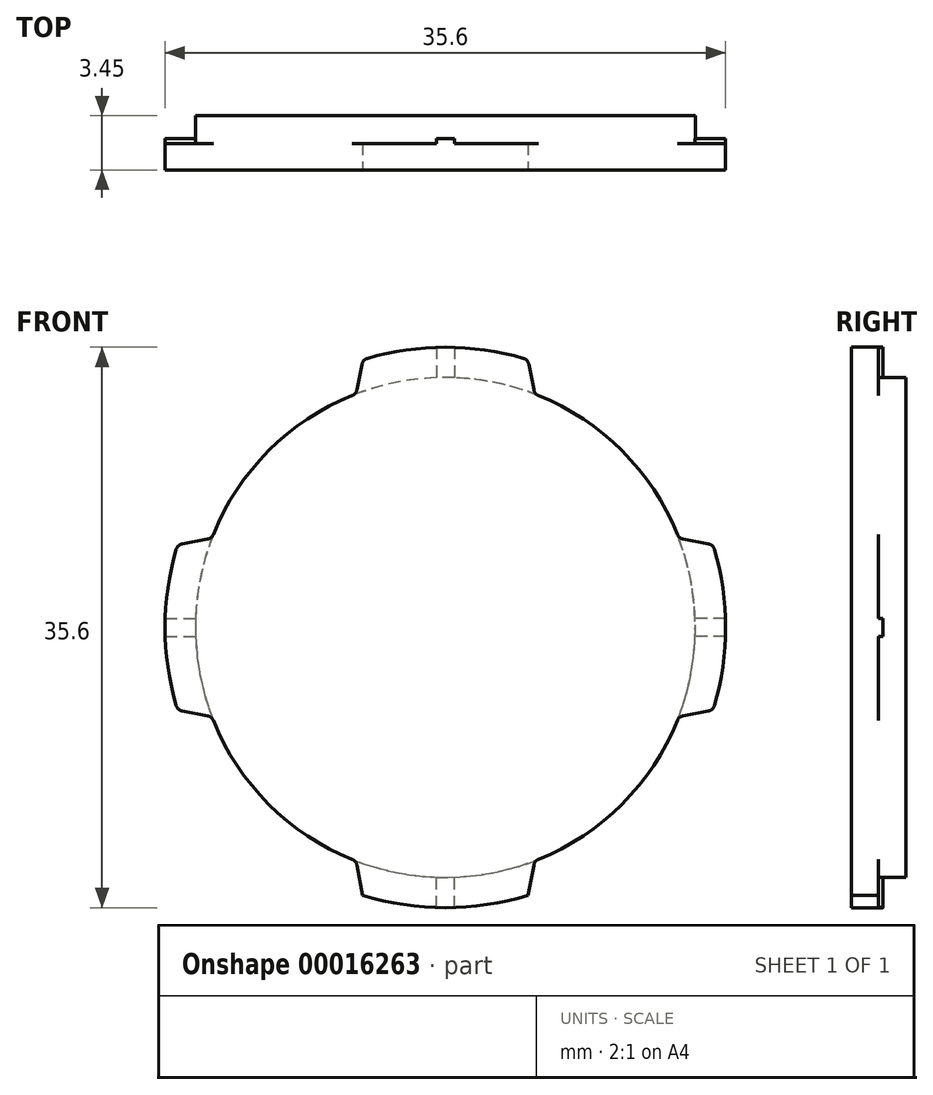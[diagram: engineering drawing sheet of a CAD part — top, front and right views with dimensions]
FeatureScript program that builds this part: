
annotation { "Feature Type Name" : "Feature", "Feature Type Description" : "" }
export const myFeature = defineFeature(function(context is Context, id is Id, definition is map)
    precondition{}
    {
        {
            var Q0;
            Q0=qCreatedBy(makeId("Front.planeOp"),FACE);
            var sketch = newSketch(context, id + "F0", { "sketchPlane" : qUnion([Q0])});
            skCircle(sketch, "E0", {"center": v(0, 0) * mm, "radius": 15.88 * mm});
            skSolve(sketch);
        }
        {
            var Q0;
            Q0=makeQuery(id+"F0.imprint","IMPRINT",FACE,{"disambiguationData":[TD([[makeQuery(id+"F0.imprint","IMPRINT",EDGE,{"derivedFrom":sQuery(id+"F0.wireOp",EDGE,"E0")}),1.0]])]});
            extrude(context, id + "F1", {"entities" : qUnion([Q0]), "depth" : 1.75 * mm});
        }
        {
            var Q0;
            Q0=makeQuery(id+"F1.opExtrude","CAP_FACE",FACE,{"disambiguationData":[OSD([sQuery(id+"F0.wireOp",EDGE,"E0")])],"isStart":false});
            var sketch = newSketch(context, id + "F2", { "sketchPlane" : qUnion([Q0])});
            skCircle(sketch, "E1", {"center": v(0, 0) * mm, "radius": 17.8 * mm});
            skSolve(sketch);
        }
        {
            var Q0;
            Q0=makeQuery(id+"F2.imprint","IMPRINT",FACE,{"disambiguationData":[TD([[makeQuery(id+"F2.imprint","IMPRINT",EDGE,{"derivedFrom":sQuery(id+"F2.wireOp",EDGE,"E1")}),1.0]])]});
            var Q1;
            Q1=makeQuery(id+"F2.imprint","IMPRINT",FACE,{"disambiguationData":[TD([[makeQuery(id+"F2.imprint","IMPRINT",EDGE,{"derivedFrom":makeQuery(id+"F1.opExtrude","CAP_EDGE",EDGE,{"disambiguationData":[OSD([sQuery(id+"F0.wireOp",EDGE,"E0")])],"isStart":false})}),1.0]])]});
            var Q2;
            Q2=sQuery(id+"F2.wireOp",EDGE,"E1");
            extrude(context, id + "F3", {"entities" : qUnion([Q0, Q1]), "operationType" : NewBodyOperationType.ADD, "surfaceEntities" : qUnion([Q2]), "depth" : 1.7 * mm});
        }
        {
            var Q0;
            Q0=makeQuery(id+"F3.opExtrude","CAP_FACE",FACE,{"disambiguationData":[OSD([sQuery(id+"F2.wireOp",EDGE,"E1")])],"isStart":false});
            var sketch = newSketch(context, id + "F4", { "sketchPlane" : qUnion([Q0])});
            skLineSegment(sketch, "E2", {"start": v(0, 17.8) * mm, "end": v(0, -17.8) * mm, "construction": true});
            skLineSegment(sketch, "E3", {"start": v(-17.8, 0) * mm, "end": v(17.8, 0) * mm, "construction": true});
            skLineSegment(sketch, "E4", {"start": v(5.25, 17) * mm, "end": v(5.75, 14.4) * mm});
            skLineSegment(sketch, "E5", {"start": v(-5.75, 14.4) * mm, "end": v(-5.25, 17) * mm});
            skCircle(sketch, "E6.0", {"center": v(0, 0) * mm, "radius": 17.8 * mm});
            skLineSegment(sketch, "E7", {"start": v(-5.75, 14.4) * mm, "end": v(5.75, 14.4) * mm, "construction": true});
            skLineSegment(sketch, "E8", {"start": v(-5.25, 17) * mm, "end": v(5.25, 17) * mm, "construction": true});
            skLineSegment(sketch, "E9.1.0", {"start": v(-14.4, -5.75) * mm, "end": v(-17, -5.25) * mm});
            skLineSegment(sketch, "E9.1.1", {"start": v(-17, -5.25) * mm, "end": v(-17, 5.25) * mm, "construction": true});
            skLineSegment(sketch, "E9.1.2", {"start": v(-14.4, -5.75) * mm, "end": v(-14.4, 5.75) * mm, "construction": true});
            skLineSegment(sketch, "E9.1.3", {"start": v(-17, 5.25) * mm, "end": v(-14.4, 5.75) * mm});
            skLineSegment(sketch, "E9.2.0", {"start": v(5.75, -14.4) * mm, "end": v(5.25, -17) * mm});
            skLineSegment(sketch, "E9.2.1", {"start": v(5.25, -17) * mm, "end": v(-5.25, -17) * mm, "construction": true});
            skLineSegment(sketch, "E9.2.2", {"start": v(5.75, -14.4) * mm, "end": v(-5.75, -14.4) * mm, "construction": true});
            skLineSegment(sketch, "E9.2.3", {"start": v(-5.25, -17) * mm, "end": v(-5.75, -14.4) * mm});
            skLineSegment(sketch, "E9.3.0", {"start": v(14.4, 5.75) * mm, "end": v(17, 5.25) * mm});
            skLineSegment(sketch, "E9.3.1", {"start": v(17, 5.25) * mm, "end": v(17, -5.25) * mm, "construction": true});
            skLineSegment(sketch, "E9.3.2", {"start": v(14.4, 5.75) * mm, "end": v(14.4, -5.75) * mm, "construction": true});
            skLineSegment(sketch, "E9.3.3", {"start": v(17, -5.25) * mm, "end": v(14.4, -5.75) * mm});
            skCircle(sketch, "E10.0", {"center": v(0, 0) * mm, "radius": 15.88 * mm});
            skSolve(sketch);
        }
        {
            var Q0;
            {var subQ2=sQuery(id+"F4.wireOp",EDGE,"E9.1.0");Q0=makeQuery(id+"F4.imprint","IMPRINT",FACE,{"disambiguationData":[TD([[makeQuery(id+"F4.imprint","IMPRINT",EDGE,{"derivedFrom":subQ2}),1.0]])]});}
            var Q1;
            {var subQ2=sQuery(id+"F4.wireOp",EDGE,"E5");Q1=makeQuery(id+"F4.imprint","IMPRINT",FACE,{"disambiguationData":[TD([[makeQuery(id+"F4.imprint","IMPRINT",EDGE,{"derivedFrom":subQ2}),1.0]])]});}
            var Q2;
            {var subQ2=sQuery(id+"F4.wireOp",EDGE,"E4");Q2=makeQuery(id+"F4.imprint","IMPRINT",FACE,{"disambiguationData":[TD([[makeQuery(id+"F4.imprint","IMPRINT",EDGE,{"derivedFrom":subQ2}),1.0]])]});}
            var Q3;
            {var subQ2=sQuery(id+"F4.wireOp",EDGE,"E9.2.0");Q3=makeQuery(id+"F4.imprint","IMPRINT",FACE,{"disambiguationData":[TD([[makeQuery(id+"F4.imprint","IMPRINT",EDGE,{"derivedFrom":subQ2}),1.0]])]});}
            extrude(context, id + "F5", {"entities" : qUnion([Q0, Q1, Q2, Q3]), "operationType" : NewBodyOperationType.REMOVE, "endBound" : BoundingType.THROUGH_ALL, "oppositeDirection" : true, "depth" : 25 * mm});
        }
        {
            var Q0;
            Q0=makeQuery(id+"F5.boolean.opBoolean","COPY",EDGE,{"derivedFrom":makeQuery(id+"F5.opExtrude","SWEPT_EDGE",EDGE,{"disambiguationData":[OSD([sQuery(id+"F4.wireOp",EDGE,"5577fbce-8590-47d3-904d-196fdd2bbf47.0"),sQuery(id+"F4.wireOp",EDGE,"E9.3.0")])]})});
            var Q1;
            Q1=makeQuery(id+"F5.boolean.opBoolean","COPY",EDGE,{"derivedFrom":makeQuery(id+"F5.opExtrude","SWEPT_EDGE",EDGE,{"disambiguationData":[OSD([sQuery(id+"F4.wireOp",EDGE,"5577fbce-8590-47d3-904d-196fdd2bbf47.0"),sQuery(id+"F4.wireOp",EDGE,"E4")])]})});
            var Q2;
            Q2=makeQuery(id+"F5.boolean.opBoolean","COPY",EDGE,{"derivedFrom":makeQuery(id+"F5.opExtrude","SWEPT_EDGE",EDGE,{"disambiguationData":[OSD([sQuery(id+"F4.wireOp",EDGE,"5577fbce-8590-47d3-904d-196fdd2bbf47.0"),sQuery(id+"F4.wireOp",EDGE,"E5")])]})});
            var Q3;
            Q3=makeQuery(id+"F5.boolean.opBoolean","COPY",EDGE,{"derivedFrom":makeQuery(id+"F5.opExtrude","SWEPT_EDGE",EDGE,{"disambiguationData":[OSD([sQuery(id+"F4.wireOp",EDGE,"5577fbce-8590-47d3-904d-196fdd2bbf47.0"),sQuery(id+"F4.wireOp",EDGE,"E9.1.3")])]})});
            var Q4;
            Q4=makeQuery(id+"F5.boolean.opBoolean","COPY",EDGE,{"derivedFrom":makeQuery(id+"F5.opExtrude","SWEPT_EDGE",EDGE,{"disambiguationData":[OSD([sQuery(id+"F4.wireOp",EDGE,"5577fbce-8590-47d3-904d-196fdd2bbf47.0"),sQuery(id+"F4.wireOp",EDGE,"E9.1.0")])]})});
            var Q5;
            Q5=makeQuery(id+"F5.boolean.opBoolean","COPY",EDGE,{"derivedFrom":makeQuery(id+"F5.opExtrude","SWEPT_EDGE",EDGE,{"disambiguationData":[OSD([sQuery(id+"F4.wireOp",EDGE,"5577fbce-8590-47d3-904d-196fdd2bbf47.0"),sQuery(id+"F4.wireOp",EDGE,"E9.2.3")])]})});
            var Q6;
            Q6=makeQuery(id+"F5.boolean.opBoolean","COPY",EDGE,{"derivedFrom":makeQuery(id+"F5.opExtrude","SWEPT_EDGE",EDGE,{"disambiguationData":[OSD([sQuery(id+"F4.wireOp",EDGE,"5577fbce-8590-47d3-904d-196fdd2bbf47.0"),sQuery(id+"F4.wireOp",EDGE,"E9.2.0")])]})});
            var Q7;
            Q7=makeQuery(id+"F5.boolean.opBoolean","COPY",EDGE,{"derivedFrom":makeQuery(id+"F5.opExtrude","SWEPT_EDGE",EDGE,{"disambiguationData":[OSD([sQuery(id+"F4.wireOp",EDGE,"5577fbce-8590-47d3-904d-196fdd2bbf47.0"),sQuery(id+"F4.wireOp",EDGE,"E9.3.3")])]})});
            fillet(context, id + "F6", {"entities" : qUnion([Q0, Q1, Q2, Q3, Q4, Q5, Q6, Q7]), "radius" : 0.5 * mm, "tangentPropagation" : true, "allowEdgeOverflow" : false});
        }
        {
            var Q0;
            {var subQ0=sQuery(id+"F2.wireOp",EDGE,"E1");var subQ3=sQuery(id+"F4.wireOp",EDGE,"E4");Q0=makeQuery(id+"F5.boolean.opBoolean","SPLIT",FACE,{"disambiguationData":[TD([makeQuery(id+"F5.opExtrude","SWEPT_FACE",FACE,{"disambiguationData":[OSD([subQ3])]})])],"derivedFrom":makeQuery(id+"F3.opExtrude","CAP_FACE",FACE,{"disambiguationData":[OSD([subQ0])],"isStart":true})});}
            var sketch = newSketch(context, id + "F7", { "sketchPlane" : qUnion([Q0])});
            skLineSegment(sketch, "E11", {"start": v(0, 17.8) * mm, "end": v(0, 0) * mm, "construction": true});
            skLineSegment(sketch, "E12.left", {"start": v(-0.58, 17.8) * mm, "end": v(-0.58, 15.86) * mm});
            skLineSegment(sketch, "E12.right", {"start": v(0.57, 17.8) * mm, "end": v(0.57, 15.86) * mm});
            skPoint(sketch, "E13.center", {"position": v(0, 0) * mm});
            skArc(sketch, "E14.0", {"start": v(-4.96, 17.1) * mm, "mid": v(0, 17.8) * mm, "end": v(4.96, 17.1) * mm});
            skCircle(sketch, "E15.0", {"center": v(0, 0) * mm, "radius": 15.88 * mm});
            skLineSegment(sketch, "E16.1.0", {"start": v(-17.8, 0.57) * mm, "end": v(-15.86, 0.57) * mm});
            skLineSegment(sketch, "E16.1.1", {"start": v(-17.8, -0.57) * mm, "end": v(-15.86, -0.57) * mm});
            skArc(sketch, "E16.1.2", {"start": v(-17.1, -4.96) * mm, "mid": v(-17.8, 0) * mm, "end": v(-17.1, 4.96) * mm});
            skLineSegment(sketch, "E16.2.0", {"start": v(-0.58, -17.8) * mm, "end": v(-0.58, -15.86) * mm});
            skLineSegment(sketch, "E16.2.1", {"start": v(0.57, -17.8) * mm, "end": v(0.57, -15.86) * mm});
            skArc(sketch, "E16.2.2", {"start": v(4.96, -17.1) * mm, "mid": v(0, -17.8) * mm, "end": v(-4.96, -17.1) * mm});
            skLineSegment(sketch, "E17.2.3.0", {"start": v(17.8, -0.58) * mm, "end": v(15.86, -0.58) * mm});
            skLineSegment(sketch, "E17.3.3.0", {"start": v(17.8, 0.57) * mm, "end": v(15.86, 0.57) * mm});
            skArc(sketch, "E17.6.3.0", {"start": v(17.1, 4.96) * mm, "mid": v(17.8, 0) * mm, "end": v(17.1, -4.96) * mm});
            skSolve(sketch);
        }
        {
            var Q0;
            Q0 = qSketchRegion(id + "F7", true);
            extrude(context, id + "F8", {"entities" : qUnion([Q0]), "operationType" : NewBodyOperationType.ADD, "depth" : .3 * mm});
        }
    });
